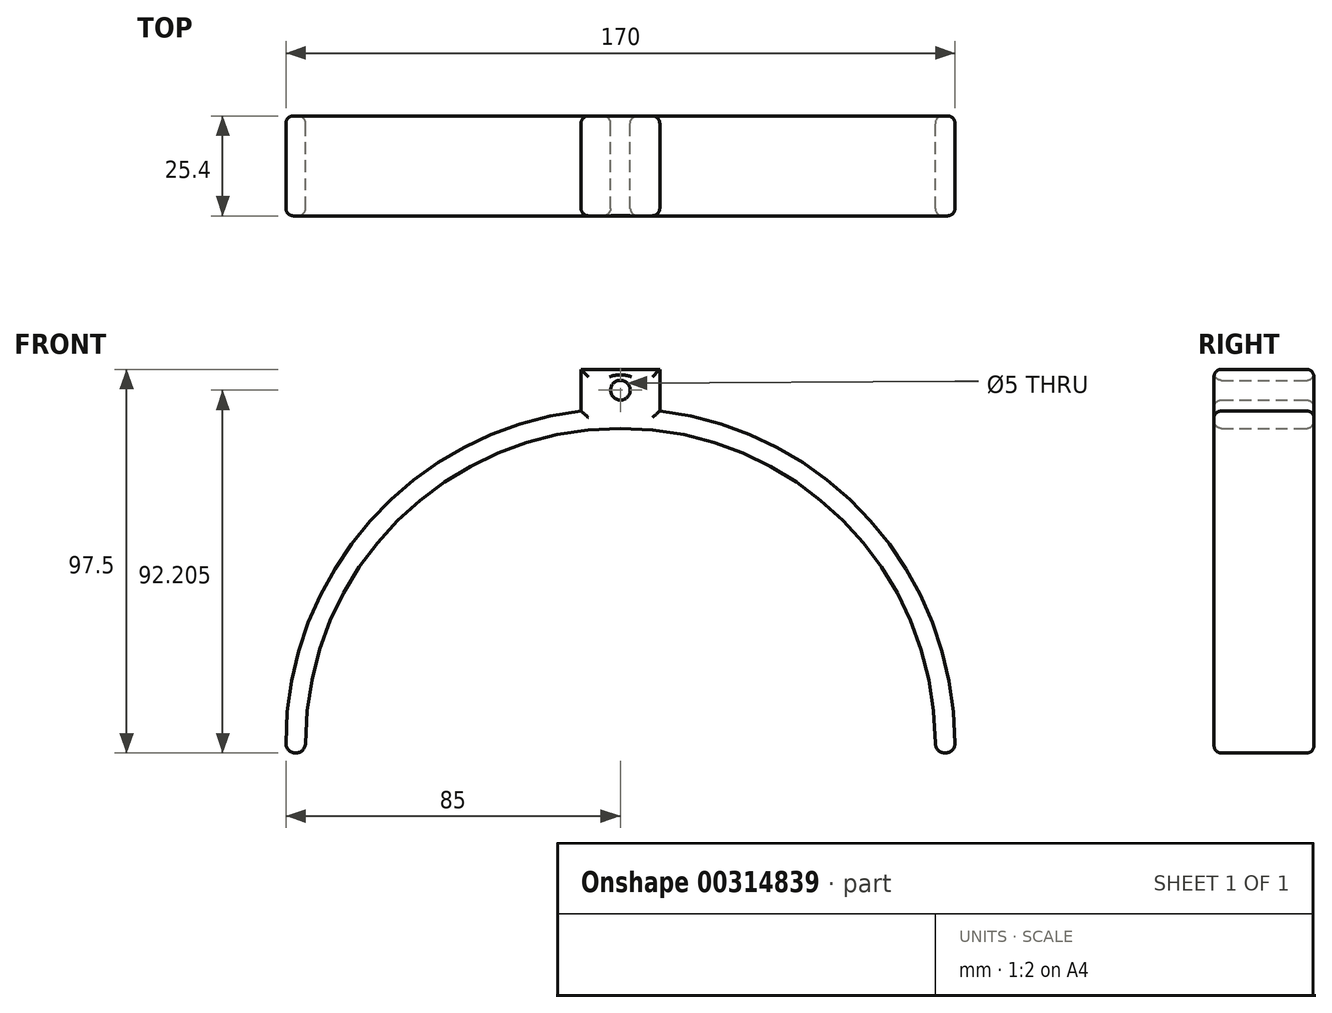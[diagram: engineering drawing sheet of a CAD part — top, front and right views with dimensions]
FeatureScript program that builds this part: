
annotation { "Feature Type Name" : "Feature", "Feature Type Description" : "" }
export const myFeature = defineFeature(function(context is Context, id is Id, definition is map)
    precondition{}
    {
        {
            var Q0;
            Q0=qCreatedBy(makeId("Front.planeOp"),FACE);
            var sketch = newSketch(context, id + "F0", { "sketchPlane" : qUnion([Q0])});
            skArc(sketch, "E0", {"start": v(80, 0) * mm, "mid": v(0, 80) * mm, "end": v(-80, 0) * mm});
            skArc(sketch, "E1", {"start": v(-10, 84.4) * mm, "mid": v(-63.54, 56.46) * mm, "end": v(-85, 0) * mm});
            skLineSegment(sketch, "E2", {"start": v(0, 0) * mm, "end": v(0, 95) * mm, "construction": true});
            skLineSegment(sketch, "E3", {"start": v(0, 95) * mm, "end": v(-10, 95) * mm});
            skLineSegment(sketch, "E4", {"start": v(0, 95) * mm, "end": v(10, 95) * mm});
            skLineSegment(sketch, "E5", {"start": v(-10, 95) * mm, "end": v(-10, 84.4) * mm});
            skLineSegment(sketch, "E6", {"start": v(10, 95) * mm, "end": v(10, 84.4) * mm});
            skLineSegment(sketch, "E7", {"start": v(-10, 84.4) * mm, "end": v(10, 95) * mm, "construction": true});
            skLineSegment(sketch, "E8", {"start": v(10, 84.4) * mm, "end": v(-10, 95) * mm, "construction": true});
            skCircle(sketch, "E9", {"center": v(0, 89.7) * mm, "radius": 2.5 * mm});
            skLineSegment(sketch, "E10", {"start": v(-80, 0) * mm, "end": v(-85, 0) * mm, "construction": true});
            skLineSegment(sketch, "E11", {"start": v(80, 0) * mm, "end": v(85, 0) * mm, "construction": true});
            skArc(sketch, "E12", {"start": v(-85, 0) * mm, "mid": v(-82.5, -2.5) * mm, "end": v(-80, 0) * mm});
            skArc(sketch, "E13", {"start": v(80, 0) * mm, "mid": v(82.5, -2.5) * mm, "end": v(85, 0) * mm});
            skArc(sketch, "E14.trimOffspring", {"start": v(85, 0) * mm, "mid": v(63.54, 56.46) * mm, "end": v(10, 84.4) * mm});
            skSolve(sketch);
        }
        {
            var Q0;
            Q0 = qSketchRegion(id + "F0", true);
            extrude(context, id + "F1", {"entities" : qUnion([Q0]), "depth" : 25.4 * mm});
        }
        {
            var Q0;
            Q0=makeQuery(id+"F1.opExtrude","CAP_FACE",FACE,{"disambiguationData":[OSD([sQuery(id+"F0.wireOp",EDGE,"E0"),sQuery(id+"F0.wireOp",EDGE,"E1"),sQuery(id+"F0.wireOp",EDGE,"E3"),sQuery(id+"F0.wireOp",EDGE,"E4"),sQuery(id+"F0.wireOp",EDGE,"E5"),sQuery(id+"F0.wireOp",EDGE,"E6"),sQuery(id+"F0.wireOp",EDGE,"E9"),sQuery(id+"F0.wireOp",EDGE,"E12"),sQuery(id+"F0.wireOp",EDGE,"E13"),sQuery(id+"F0.wireOp",EDGE,"E14.trimOffspring")])],"isStart":false});
            fillet(context, id + "F2", {"entities" : qUnion([Q0]), "radius" : 1.9 * mm, "tangentPropagation" : true, "allowEdgeOverflow" : false});
        }
        {
            var Q0;
            Q0=makeQuery(id+"F1.opExtrude","CAP_FACE",FACE,{"disambiguationData":[OSD([sQuery(id+"F0.wireOp",EDGE,"E0"),sQuery(id+"F0.wireOp",EDGE,"E1"),sQuery(id+"F0.wireOp",EDGE,"E3"),sQuery(id+"F0.wireOp",EDGE,"E4"),sQuery(id+"F0.wireOp",EDGE,"E5"),sQuery(id+"F0.wireOp",EDGE,"E6"),sQuery(id+"F0.wireOp",EDGE,"E9"),sQuery(id+"F0.wireOp",EDGE,"E12"),sQuery(id+"F0.wireOp",EDGE,"E13"),sQuery(id+"F0.wireOp",EDGE,"E14.trimOffspring")])],"isStart":true});
            fillet(context, id + "F3", {"entities" : qUnion([Q0]), "radius" : 1.9 * mm, "tangentPropagation" : true, "allowEdgeOverflow" : false});
        }
    });
